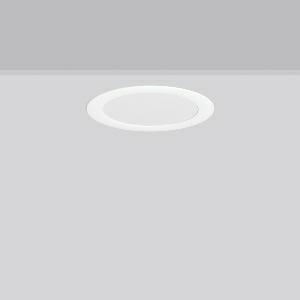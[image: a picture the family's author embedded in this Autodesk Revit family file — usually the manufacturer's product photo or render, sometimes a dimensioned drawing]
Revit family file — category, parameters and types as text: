
# Revit family: toledo_flat_round_e_901715_002_1_19_9782
name_source: partatom
category: Lighting Fixtures
units: mm (PartAtom-declared; Revit-internal decimal feet)

## family parameters
Cut with Voids When Loaded = No
Host = Face
Light Source = No
Part Type = Normal
Room Calculation Point = No
Round Connector Dimension = Use Diameter
Shared = No

## types (1)
- TOLEDO FLAT round E (1 x LED Modul 840, 1800 lm, 4000)
    Apparent Load = 17 VA
    CIE Flux Codes = 48 79 96 100 100
    Color Rendering = 80
    Color Temperature = 4000
    Default Elevation = 1800 mm  [stored 5.90551 ft]
    Description = Series: TOLEDO FLAT round
Ultra thin recessed downlight. Housing: die-cast aluminium. Light guide and diffuser made of non-yellowing PMMA, opal matt. Ceiling installation with spring system. Mounting depth depends on ceiling strength. Including separate LED converter with connecting cable 250 mm.Connected HF motion detector in a separate ballast box. Adjustable dim functions Soft Start, Corridor, Permanent. Wireless networking, sensor configuration and communication via Bluetooth. Operation via an Android / iOS device, free app available for download. master/slave Brightness sensor without function. Not suitable for metal ceilings.Versions with movement sensor not suitable for surface-mounted housing. Suitable for through-wiring with separately available accessories. Retrofittable decorative cylinders made of chintz fabric as accessory, optional with satin finish plastic diffuser. Through-wiring box (5 pole) available as accessory. 
Colour: white
Diameter: 255 mm
Height: 3 mm
Cut-out diameter: 234 mm
Recess height: 55-76 mm
Luminaire: recess height: 31-51 mm
Lamp: LED
Socket: without socket
Colour temperature: 4000K
Colour rendering index (CRI): 80
System power: 17 W
Rated luminous flux: 1800 lm
Luminous efficiency: 106 lm/W
Control gear: Dimmable Bluetooth converter
Protection class: I
Type of protection: IP 54
    Height = 0 mm  [stored 0 ft]
    Lamp = 1 x LED Modul 840
    Lamp Light Flux = 1800 lm
    Lamp count = 1
    Length = 255 mm
    Lifetime = 50000 h
    Luminous efficacy = 106 lm/W
    Manufacturer = RZB
    ModVariant = No
    Model = 901715.002.1.19
    Mounting Place = Ceiling
    Mounting Type = Recessed
    Number of Poles = 1
    OnlyDefault = Yes
    Power Factor = 1
    Product Name = TOLEDO FLAT round E
    Product group = Recessed downlights
    ProductGroupID = 402
    Protection Class = Protection class I
    Protection Degree = IP 20
    RLX_Detail_Level = 1
    RLX_Emergency_Light_Flux = 0 lm
    RLX_Emergency_Type = 0
    RLX_Emergency_Type_DB = No
    RlxData = <blob elided: 30609 chars, md5=d1360963>
    Socket = socket
    Standby Power = 0 W
    System Light Flux = 1800 lm
    System Power = 17 W
    Type Comments = Product without accessories
    Type Image = 901453.002.jpg
    URL = http://relux.com
    VarID = ---
    Voltage = 230 V
    Voltage Range = 220-240 V
    Weight = 0.00 kg
    Width = 0 mm  [stored 0 ft]

note: [stored X ft] marks values corroborated as IEEE doubles in the binary element streams (Revit-internal decimal feet)

## geometry (parser evidence)
native form markers: Blend x4, Sweep x11
no freeform markers — native parametric forms only
